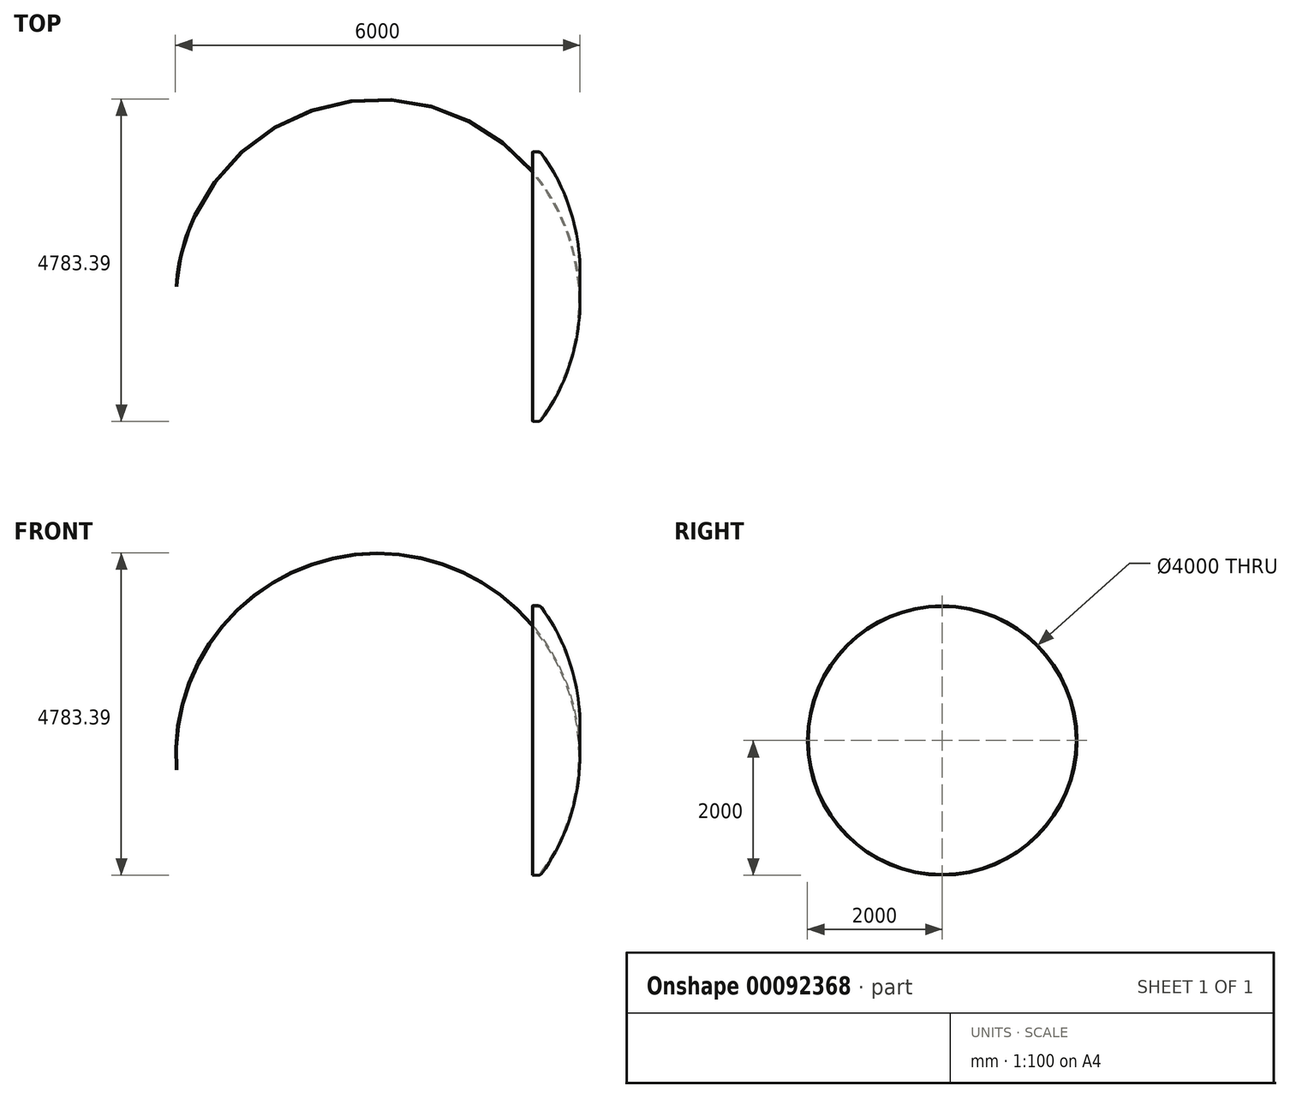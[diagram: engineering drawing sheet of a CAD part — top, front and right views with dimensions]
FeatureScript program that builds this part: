
annotation { "Feature Type Name" : "Feature", "Feature Type Description" : "" }
export const myFeature = defineFeature(function(context is Context, id is Id, definition is map)
    precondition{}
    {
        {
            var Q0;
            Q0=qCreatedBy(makeId("Front.planeOp"),FACE);
            var sketch = newSketch(context, id + "F0", { "sketchPlane" : qUnion([Q0])});
            skLineSegment(sketch, "E0", {"start": v(895, 2000) * mm, "end": v(979.63, 2000) * mm});
            skArc(sketch, "E1.trimOffspring", {"start": v(1595, 0) * mm, "mid": v(1489.15, 1034.62) * mm, "end": v(1036.42, 1970.93) * mm});
            skPoint(sketch, "E2.center.orphan", {"position": v(0, 0) * mm});
            skLineSegment(sketch, "E3", {"start": v(1595, 0) * mm, "end": v(895, 0) * mm, "construction": true});
            skLineSegment(sketch, "E4", {"start": v(895, 0) * mm, "end": v(895, 974.56) * mm, "construction": true});
            skLineSegment(sketch, "E5", {"start": v(895, 0) * mm, "end": v(895, -975) * mm, "construction": true});
            skLineSegment(sketch, "E6", {"start": v(895, 2000) * mm, "end": v(895, 948.65) * mm, "construction": true});
            skPoint(sketch, "E7.trimOffspring.end.orphan", {"position": v(895, -2000) * mm});
            skPoint(sketch, "E7.trimOffspring.start.orphan", {"position": v(895, -948.65) * mm});
            skLineSegment(sketch, "E8", {"start": v(1579.96, 0) * mm, "end": v(1595, 0) * mm});
            skLineSegment(sketch, "E9", {"start": v(895, 2000) * mm, "end": v(895, 1985) * mm});
            skArc(sketch, "E10.0", {"start": v(1579.96, 0) * mm, "mid": v(1474.87, 1030.01) * mm, "end": v(1024.25, 1962.16) * mm});
            skLineSegment(sketch, "E10.1", {"start": v(895, 1985) * mm, "end": v(979.63, 1985) * mm});
            skPoint(sketch, "E11.visualSharp", {"position": v(1015.2, 2000) * mm});
            skArc(sketch, "E11.filletArc", {"start": v(1036.42, 1970.93) * mm, "mid": v(1011.53, 1992.31) * mm, "end": v(979.63, 2000) * mm});
            skPoint(sketch, "E12.visualSharp", {"position": v(1007.62, 1985) * mm});
            skArc(sketch, "E12.filletArc", {"start": v(1024.25, 1962.16) * mm, "mid": v(1004.7, 1978.96) * mm, "end": v(979.63, 1985) * mm});
            skSolve(sketch);
        }
        {
            var Q0;
            Q0=makeQuery(id+"F0.imprint","IMPRINT",FACE,{"disambiguationData":[TD([[makeQuery(id+"F0.imprint","IMPRINT",EDGE,{"derivedFrom":sQuery(id+"F0.wireOp",EDGE,"E0")}),-1.0]])]});
            var Q1;
            Q1=sQuery(id+"F0.wireOp",EDGE,"E3");
            revolve(context, id + "F1", {"entities" : qUnion([Q0]), "axis" : qUnion([Q1]), "revolveType" : RevolveType.FULL});
        }
        {
            var Q0;
            Q0=makeQuery(id+"F1.opRevolve","SWEPT_EDGE",EDGE,{"disambiguationData":[OSD([sQuery(id+"F0.wireOp",EDGE,"E0"),sQuery(id+"F0.wireOp",EDGE,"E9")])]});
            var Q1;
            Q1=makeQuery(id+"F1.opRevolve","SWEPT_EDGE",EDGE,{"disambiguationData":[OSD([sQuery(id+"F0.wireOp",EDGE,"E9"),sQuery(id+"F0.wireOp",EDGE,"2daf78f5-6c8c-4334-9f63-1748af5aa70e")])]});
            chamfer(context, id + "F2", {"entities" : qUnion([Q0, Q1]), "width" : 5 * mm, "tangentPropagation" : true});
        }
    });
